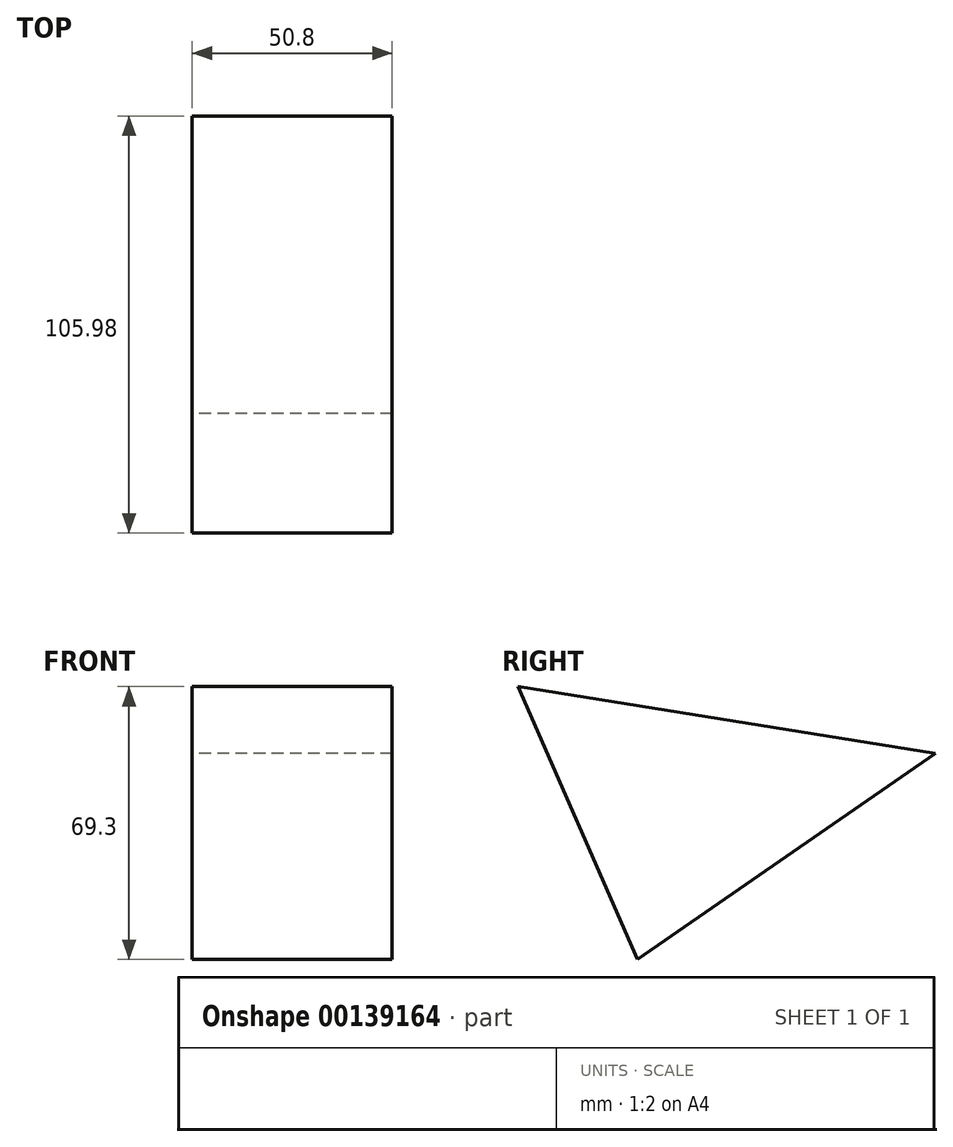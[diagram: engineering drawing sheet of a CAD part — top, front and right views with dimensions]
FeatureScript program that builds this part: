
annotation { "Feature Type Name" : "Feature", "Feature Type Description" : "" }
export const myFeature = defineFeature(function(context is Context, id is Id, definition is map)
    precondition{}
    {
        {
            var Q0;
            Q0=qCreatedBy(makeId("Right.planeOp"),FACE);
            var sketch = newSketch(context, id + "F0", { "sketchPlane" : qUnion([Q0])});
            skLineSegment(sketch, "E0", {"start": v(-59.66, 35.44) * mm, "end": v(-29.3, -33.86) * mm});
            skLineSegment(sketch, "E1", {"start": v(-29.3, -33.86) * mm, "end": v(46.32, 18.42) * mm});
            skLineSegment(sketch, "E2", {"start": v(46.32, 18.42) * mm, "end": v(-59.66, 35.44) * mm});
            skSolve(sketch);
        }
        {
            var Q0;
            Q0=makeQuery(id+"F0.imprint","IMPRINT",FACE,{"disambiguationData":[TD([[makeQuery(id+"F0.imprint","IMPRINT",EDGE,{"derivedFrom":sQuery(id+"F0.wireOp",EDGE,"E0")}),1.0]])]});
            extrude(context, id + "F1", {"entities" : qUnion([Q0]), "depth" : 50.8 * mm});
        }
    });
